# Revit family: RFll-TY3551_Metric
name_source: partatom
category: Sprinklers
units: mm (PartAtom-declared; Revit-internal decimal feet)

## family parameters
Always vertical = Yes
Cut with Voids When Loaded = No
Maintain Annotation Orientation = No
OmniClass Number = 23.65.70.17.11.24
OmniClass Title = Fire Fighting Sprinkler Heads
Part Type = Normal
Room Calculation Point = No
Round Connector Dimension = Use Diameter
Shared = No
Work Plane-Based = No

## types (7) — shared parameters
COBie = Yes
COBie.Component.Name = Sprinklers:Concealed Flush
COBie.Type = Yes
COBie.Type.AssetType = Fixed
COBie.Type.Category = Pr_70_55_97_84:Sprinklers
COBie.Type.DurationUnit = year
COBie.Type.Manufacturer = Tyco Fire Protection Products
COBie.Type.Material = Bronze
COBie.Type.Shape = Cylinder
COBie.Type.Size = 1/2"(DN15)
COBie.Type.WarrantyGuarantorParts = http://tycofsbp.com
Coverage = Standard
Coverage_ = Standard
K-Factor = 80.64
Manufacturer = Tyco Fire Protection Products
Manufacturer URL = www.tyco-fire.com
Material_ = Bronze
Model = RFII
Nominal Diameter 1 = 15 mm
Orifice = Extra Large
Orifice Size = 0 mm
Outside Diameter 1 = 21 mm
Response = Standard
Response_ = Standard
SIN No = TY3551
Takeout 1 = 62 mm
Technical Data Sheet No = TFP181
zero-valued in all types: COBie.Type.NominalHeight, COBie.Type.NominalLength, COBie.Type.NominalWidth, COBie.Type.ReplacementCost, Default Elevation, Style Id

## per-type parameters (varying)
| type | COBie.Component.Description | COBie.Type.Finish | COBie.Type.ModelNumber | COBie.Type.ModelReference | Description | Finish_ | Part No | Temperature Rating |
| RFll Concealed Pendent 68°C 1/2" NPT Brass_51-790-1-155 | RFII Concealed Flush SC SR 155°F K5.6 1/2 NPT | Natural Brass | 51-790-1-155 | RFII Concealed Flush SC SR 155°F K5.6 1/2 NPT | Tyco RF II Pendent K5.6/80 68°C 1/2" NPT Brass Plated TY3551 | Natural Brass | 51-790-1-155 | 68 °C |
| RFll Concealed Pendent 93°C 1/2" NPT Brass_51-790-1-200 | RFII Concealed Flush SC SR 200°F K5.6 1/2 NPT | Natural Brass | 51-790-1-200 | RFII Concealed Flush SC SR 200°F K5.6 1/2 NPT | Tyco RF II Pendent K5.6/80 93°C 1/2" NPT Brass Plated TY3551 | Natural Brass | 51-790-1-200 | 93 °C |
| RFll Concealed Pendent 68°C 1/2" NPT Pure White_51-790-3-155 | RFII Concealed Flush SC SR 155°F K5.6 1/2 NPT | Pure White | 51-790-3-155 | RFII Concealed Flush SC SR 155°F K5.6 1/2 NPT | Tyco RF II Pendent K5.6/80 68°C 1/2" NPT Brass Plated TY3551 | Pure White | 51-790-3-155 | 68 °C |
| RFll Concealed Pendent 68°C 1/2" NPT Chrome_51-790-9-155 | RFII Concealed Flush SC SR 155°F K5.6 1/2 NPT | Chrome | 51-790-9-155 | RFII Concealed Flush SC SR 155°F K5.6 1/2 NPT | Tyco RF II Pendent K5.6/80 68°C 1/2" NPT Brass Plated TY3551 | Chrome | 51-790-9-155 | 68 °C |
| RFll Concealed Pendent 68°C 1/2" NPT Gray White_51-790-0-155 | RFII Concealed Flush SC SR 155°F K5.6 1/2 NPT | Gray White | 51-790-0-155 | RFII Concealed Flush SC SR 155°F K5.6 1/2 NPT | Tyco RF II Pendent K5.6/80 68°C 1/2" NPT Brass Plated TY3551 | Gray White | 51-790-0-155 | 68 °C |
| RFll Concealed Pendent 68°C 1/2" NPT Signal White_51-790-4-155 | RFII Concealed Flush SC SR 155°F K5.6 1/2 NPT | Signal White | 51-790-4-155 | RFII Concealed Flush SC SR 155°F K5.6 1/2 NPT | Tyco RF II Pendent K5.6/80 68°C 1/2" NPT Brass Plated TY3551 | Signal White | 51-790-4-155 | 68 °C |
| RFll Concealed Pendent 68°C 1/2" NPT Chrome_51-790-8-155 | RFII Concealed Flush SC SR 155°F K5.6 1/2 NPT | Chrome | 51-790-8-155 | RFII Concealed Flush SC SR 155°F K5.6 1/2 NPT | Tyco RF II Pendent K5.6/80 68°C 1/2" NPT Brass Plated TY3551 | Chrome | 51-790-8-155 | 68 °C |

## geometry (parser evidence)
native form markers: Blend x4, Sweep x23
no freeform markers — native parametric forms only
